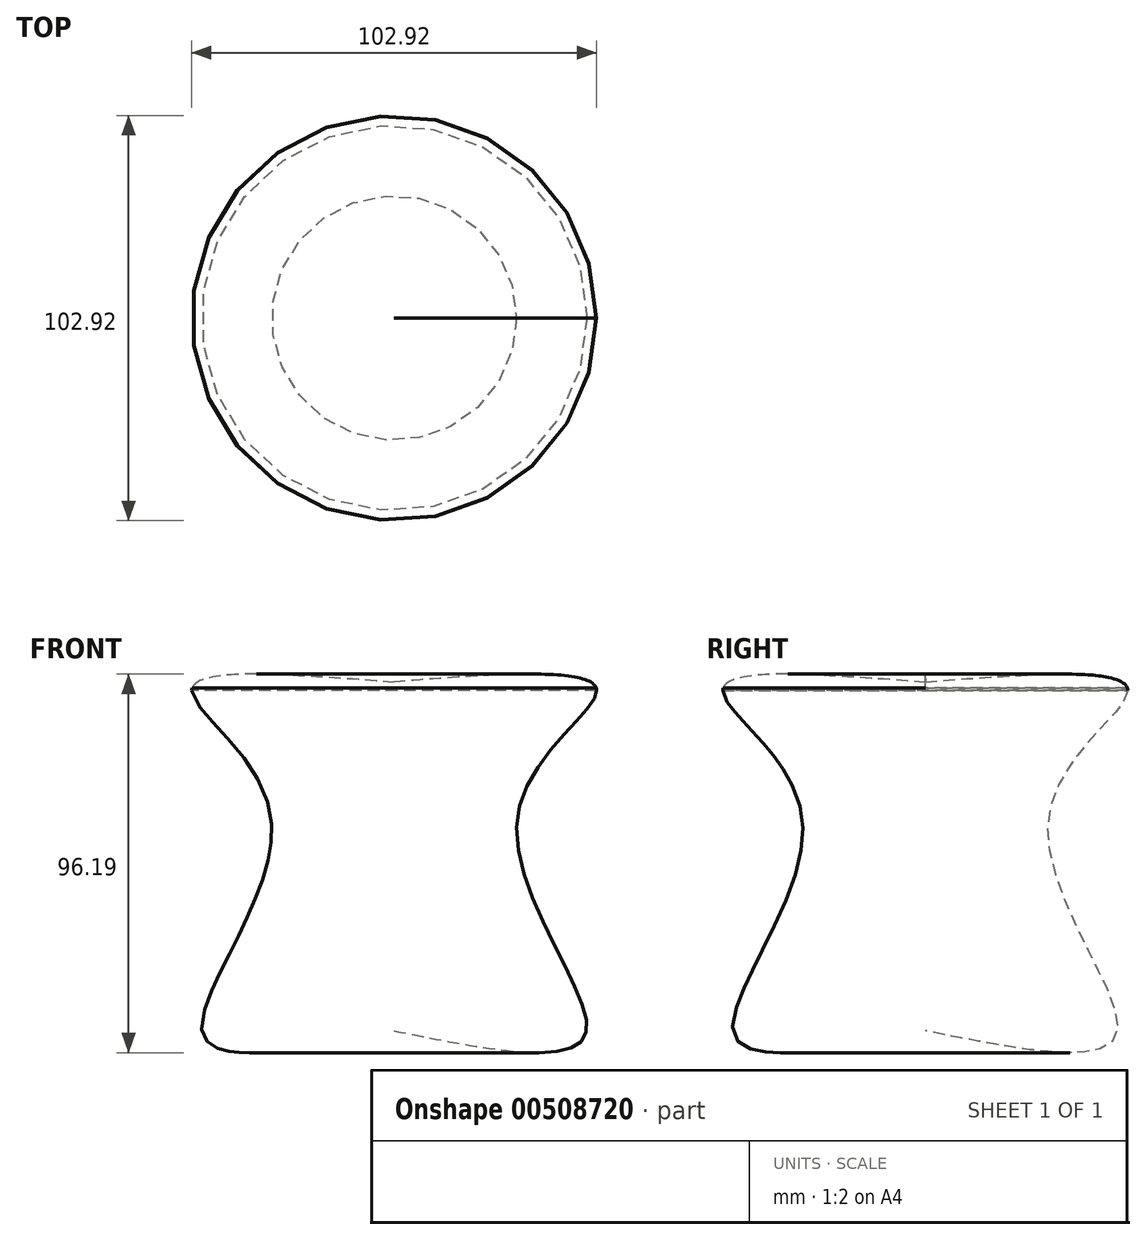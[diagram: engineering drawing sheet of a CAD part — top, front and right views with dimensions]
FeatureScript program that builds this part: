
annotation { "Feature Type Name" : "Feature", "Feature Type Description" : "" }
export const myFeature = defineFeature(function(context is Context, id is Id, definition is map)
    precondition{}
    {
        {
            var Q0;
            Q0=qCreatedBy(makeId("Front.planeOp"),FACE);
            var sketch = newSketch(context, id + "F0", { "sketchPlane" : qUnion([Q0])});
            skLineSegment(sketch, "E0", {"start": v(0, 64.38) * mm, "end": v(0, -74.9) * mm});
            skFitSpline(sketch, "E1", {"points": [v(0, -56.04) * mm, v(48.76, -56.58) * mm, v(31.25, -1.89) * mm, v(51.45, 30.44) * mm, v(0, 32.6) * mm], "startDerivative": vector(279.01, -56.73) * mm, "endDerivative": vector(-298.47, -23.38) * mm});
            skFitSpline(sketch, "E2.0", {"points": [v(-1.27, -62.26) * mm, v(1.64, -62.85) * mm, v(7.48, -64.04) * mm, v(16.07, -65.67) * mm, v(22.9, -66.78) * mm, v(28.09, -67.44) * mm, v(31.82, -67.79) * mm, v(35.37, -67.97) * mm, v(38.75, -67.96) * mm, v(41.96, -67.71) * mm, v(45.05, -67.15) * mm, v(47.55, -66.32) * mm, v(49.51, -65.3) * mm, v(50.93, -64.33) * mm, v(52.26, -63.11) * mm, v(53.43, -61.65) * mm, v(54.2, -60.25) * mm, v(54.65, -59.07) * mm, v(54.92, -58.15) * mm, v(55.12, -57.24) * mm, v(55.27, -56.06) * mm, v(55.32, -54.62) * mm, v(55.2, -52.98) * mm, v(54.85, -50.88) * mm, v(54.16, -48.34) * mm, v(53.04, -45.3) * mm, v(51.7, -42.19) * mm, v(50.19, -39) * mm, v(48.56, -35.73) * mm, v(46.3, -31.26) * mm, v(43.46, -25.54) * mm, v(40.94, -19.8) * mm, v(39.34, -15.35) * mm, v(38.38, -12.12) * mm, v(37.73, -9.05) * mm, v(37.45, -6.67) * mm, v(37.4, -4.89) * mm, v(37.44, -3.83) * mm, v(37.5, -3.01) * mm, v(37.6, -2.22) * mm, v(37.79, -1.24) * mm, v(38.09, -0.05) * mm, v(38.6, 1.54) * mm, v(39.47, 3.54) * mm, v(40.8, 5.95) * mm, v(42.37, 8.33) * mm, v(44.14, 10.67) * mm, v(46.04, 12.94) * mm, v(47.99, 15.13) * mm, v(49.93, 17.24) * mm, v(51.8, 19.27) * mm, v(53.27, 20.92) * mm, v(54.36, 22.26) * mm, v(55.14, 23.29) * mm, v(55.88, 24.37) * mm, v(56.57, 25.54) * mm, v(57.19, 26.9) * mm, v(57.6, 28.24) * mm, v(57.79, 29.5) * mm, v(57.82, 30.36) * mm, v(57.78, 31.09) * mm, v(57.7, 31.82) * mm, v(57.5, 32.72) * mm, v(57.1, 33.76) * mm, v(56.45, 35.03) * mm, v(55.4, 36.35) * mm, v(54.06, 37.49) * mm, v(52.72, 38.3) * mm, v(51.4, 38.92) * mm, v(49.63, 39.54) * mm, v(47.4, 40.08) * mm, v(44.51, 40.5) * mm, v(41.4, 40.77) * mm, v(38.03, 40.91) * mm, v(34.42, 40.94) * mm, v(30.57, 40.88) * mm, v(25.17, 40.7) * mm, v(17.97, 40.3) * mm, v(8.85, 39.66) * mm, v(2.61, 39.17) * mm, v(-0.5, 38.92) * mm]});
            skFitSpline(sketch, "E3", {"points": [v(51.45, 30.44) * mm, v(51.45, 35.29) * mm, v(56.37, 35.06) * mm], "startDerivative": vector(-2.44, 12.27) * mm, "endDerivative": vector(12.24, -3) * mm});
            skFitSpline(sketch, "E4.trimOffspring", {"points": [v(-1.27, -62.26) * mm, v(1.64, -62.85) * mm, v(7.48, -64.04) * mm, v(16.07, -65.67) * mm, v(22.9, -66.78) * mm, v(28.09, -67.44) * mm, v(31.82, -67.79) * mm, v(35.37, -67.97) * mm, v(38.75, -67.96) * mm, v(41.96, -67.71) * mm, v(45.05, -67.15) * mm, v(47.55, -66.32) * mm, v(49.51, -65.3) * mm, v(50.93, -64.33) * mm, v(52.26, -63.11) * mm, v(53.43, -61.65) * mm, v(54.2, -60.25) * mm, v(54.65, -59.07) * mm, v(54.92, -58.15) * mm, v(55.12, -57.24) * mm, v(55.27, -56.06) * mm, v(55.32, -54.62) * mm, v(55.2, -52.98) * mm, v(54.85, -50.88) * mm, v(54.16, -48.34) * mm, v(53.04, -45.3) * mm, v(51.7, -42.19) * mm, v(50.19, -39) * mm, v(48.56, -35.73) * mm, v(46.3, -31.26) * mm, v(43.46, -25.54) * mm, v(40.94, -19.8) * mm, v(39.34, -15.35) * mm, v(38.38, -12.12) * mm, v(37.73, -9.05) * mm, v(37.45, -6.67) * mm, v(37.4, -4.89) * mm, v(37.44, -3.83) * mm, v(37.5, -3.01) * mm, v(37.6, -2.22) * mm, v(37.79, -1.24) * mm, v(38.09, -0.05) * mm, v(38.6, 1.54) * mm, v(39.47, 3.54) * mm, v(40.8, 5.95) * mm, v(42.37, 8.33) * mm, v(44.14, 10.67) * mm, v(46.04, 12.94) * mm, v(47.99, 15.13) * mm, v(49.93, 17.24) * mm, v(51.8, 19.27) * mm, v(53.27, 20.92) * mm, v(54.36, 22.26) * mm, v(55.14, 23.29) * mm, v(55.88, 24.37) * mm, v(56.57, 25.54) * mm, v(57.19, 26.9) * mm, v(57.6, 28.24) * mm, v(57.79, 29.5) * mm, v(57.82, 30.36) * mm, v(57.78, 31.09) * mm, v(57.7, 31.82) * mm, v(57.5, 32.72) * mm, v(57.1, 33.76) * mm, v(56.45, 35.03) * mm, v(55.4, 36.35) * mm, v(54.06, 37.49) * mm, v(52.72, 38.3) * mm, v(51.4, 38.92) * mm, v(49.63, 39.54) * mm, v(47.4, 40.08) * mm, v(44.51, 40.5) * mm, v(41.4, 40.77) * mm, v(38.03, 40.91) * mm, v(34.42, 40.94) * mm, v(30.57, 40.88) * mm, v(25.17, 40.7) * mm, v(17.97, 40.3) * mm, v(8.85, 39.66) * mm, v(2.61, 39.17) * mm, v(-0.5, 38.92) * mm]});
            skSolve(sketch);
        }
        {
            var Q0;
            {var subQ0=sQuery(id+"F0.wireOp",EDGE,"E1");Q0=makeQuery(id+"F0.imprint","IMPRINT",FACE,{"disambiguationData":[TD([[makeQuery(id+"F0.imprint","IMPRINT",EDGE,{"derivedFrom":subQ0}),1.0]])]});}
            var Q1;
            {var subQ3=sQuery(id+"F0.wireOp",EDGE,"E0");var subQ5=sQuery(id+"F0.wireOp",EDGE,"E1");var subQ8=makeQuery(id+"F0.imprint","INTERSECT",VERTEX,{"derivedFrom":[subQ3,subQ5]});Q1=makeQuery(id+"F0.imprint","IMPRINT",FACE,{"disambiguationData":[TD([[makeQuery(id+"F0.imprint","IMPRINT",EDGE,{"disambiguationData":[TD([[subQ8,-1.0]])],"derivedFrom":subQ3}),1.0]])]});}
            var Q2;
            Q2=sQuery(id+"F0.wireOp",EDGE,"E0");
            revolve(context, id + "F1", {"entities" : qUnion([Q0, Q1]), "axis" : qUnion([Q2]), "revolveType" : RevolveType.FULL});
        }
    });
